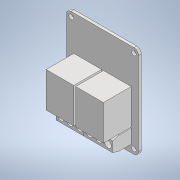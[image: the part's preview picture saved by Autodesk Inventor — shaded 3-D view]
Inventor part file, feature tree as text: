
AUTODESK INVENTOR PART (.ipt)
format: ipt  version: 2020.2 (Build 242310000, 310)  size: 248,832 bytes
history: native  units: mm
features: extrude x5, sketch x5, chamfer x4
ambient origin geometry x8: Origin, YZ Plane, XZ Plane, XY Plane, X Axis, Y Axis, Z Axis, Center Point
bodies: Solid1 (feature_tree)
feature tree (14):
  extrude  "Extrusion1"  Depth=39.0mm
  extrude  "Extrusion2"  Depth=2.5mm
  extrude  "Extrusion3"  Depth=2.5mm
  chamfer  "Chamfer1"  Distance=2.5mm
  chamfer  "Chamfer2"  Distance=2.55mm
  chamfer  "Chamfer3"  Distance=2.55mm
  chamfer  "Chamfer4"  Distance=2.55mm
  extrude  "Extrusion4"  Depth=0.5mm
  extrude  "Extrusion5"  Depth=0.5mm
  sketch  "Sketch1"  dims[d0=50.0mm d1=39.0mm]
  sketch  "Sketch2"  dims[d2=2.5mm d3=2.55mm]
  sketch  "Sketch3"  dims[d4=2.55mm d5=2.5mm]
  sketch  "Sketch4"  dims[d6=2.5mm]
  sketch  "Sketch5"  dims[d7=2.5mm d8=2.5mm d9=2.55mm d10=2.55mm d11=2.55mm d12=2.55mm d13=2.55mm d14=2.55mm d15=2.5mm d16=1.5mm d17=0.0mm d18=15.0mm d19=19.0mm d20=20.0mm d22=16.0mm d23=10.0mm d25=10.0mm d27=4.0mm d28=39.0mm d29=12.0mm d30=15.0mm d31=0.0mm d32=15.0mm d33=7.5mm d34=0.5mm d35=0.5mm d36=15.0mm d37=7.5mm d38=0.5mm d39=0.5mm d40=10.0mm d41=0.0mm d42=1.0mm d43=3.5mm d44=45.0deg d45=1.0mm d46=3.5mm d47=45.0deg d48=1.0mm d49=3.5mm d50=45.0deg d51=1.0mm d52=3.5mm d53=45.0deg d54=0.5mm d55=0.25mm d56=3.5mm d57=2.5mm d58=5.5mm d59=2.75mm d60=30.0mm d62=5.0mm d63=10.0mm d65=10.0mm d68=3.0mm d69=0.0mm d71=4.1mm d72=4.5mm d73=4.5mm d74=0.55mm d75=30.0mm d77=4.9mm d78=10.0mm d80=10.0mm d83=3.0mm d84=0.0mm d85=0.5mm d86=0.25mm]
